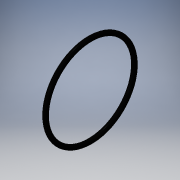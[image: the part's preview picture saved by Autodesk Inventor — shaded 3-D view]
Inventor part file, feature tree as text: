
AUTODESK INVENTOR PART (.ipt)
format: ipt  version: 2016 (Build 200138000, 138)  size: 127,488 bytes
history: native  units: in
note: dims shown in document units (in); Inventor stores cm internally (conversion verified against a paired STEP export)
features: revolve x1, sketch x1
ambient origin geometry x8: Origin, YZ Plane, XZ Plane, XY Plane, X Axis, Y Axis, Z Axis, Center Point
bodies: Solid1 (feature_tree)
feature tree (2):
  revolve  "Revolution1"  Angle=90.0deg
  sketch  "Sketch1"  dims[d0=0.139in d2=90.0deg d3=2.484in]
